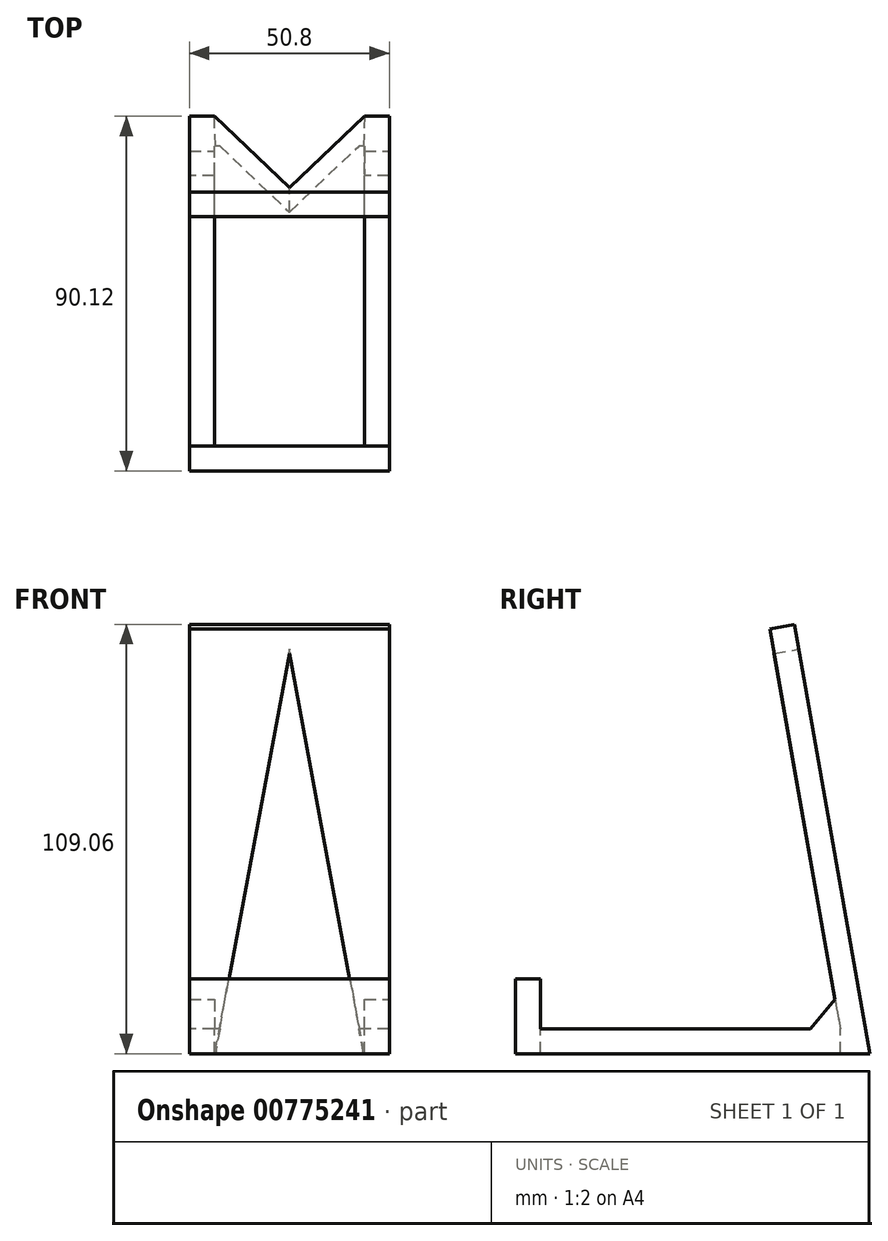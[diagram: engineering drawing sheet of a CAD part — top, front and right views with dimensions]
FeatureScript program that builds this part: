
annotation { "Feature Type Name" : "Feature", "Feature Type Description" : "" }
export const myFeature = defineFeature(function(context is Context, id is Id, definition is map)
    precondition{}
    {
        {
            var Q0;
            Q0=qCreatedBy(makeId("Right.planeOp"),FACE);
            var sketch = newSketch(context, id + "F0", { "sketchPlane" : qUnion([Q0])});
            skLineSegment(sketch, "E0", {"start": v(-39.61, -22.49) * mm, "end": v(36.59, -22.49) * mm});
            skLineSegment(sketch, "E1", {"start": v(36.59, -22.49) * mm, "end": v(18.67, 79.11) * mm});
            skLineSegment(sketch, "E2", {"start": v(-39.61, -22.49) * mm, "end": v(-39.61, -9.79) * mm});
            skLineSegment(sketch, "E3.0", {"start": v(-45.96, -28.84) * mm, "end": v(-45.96, -9.79) * mm});
            skLineSegment(sketch, "E3.1", {"start": v(-45.96, -28.84) * mm, "end": v(44.16, -28.84) * mm});
            skLineSegment(sketch, "E3.2", {"start": v(44.16, -28.84) * mm, "end": v(24.93, 80.22) * mm});
            skLineSegment(sketch, "E4", {"start": v(-45.96, -9.79) * mm, "end": v(-39.61, -9.79) * mm});
            skLineSegment(sketch, "E5", {"start": v(18.67, 79.11) * mm, "end": v(24.93, 80.22) * mm});
            skSolve(sketch);
        }
        {
            var Q0;
            Q0 = qSketchRegion(id + "F0", true);
            extrude(context, id + "F1", {"entities" : qUnion([Q0]), "depth" : 50.8 * mm, "offsetDistance" : 25.4 * mm});
        }
        {
            var Q0;
            Q0=makeQuery(id+"F1.opExtrude","SWEPT_FACE",FACE,{"disambiguationData":[OSD([sQuery(id+"F0.wireOp",EDGE,"E0")])]});
            var sketch = newSketch(context, id + "F2", { "sketchPlane" : qUnion([Q0])});
            skLineSegment(sketch, "E6.bottom", {"start": v(6.35, -39.61) * mm, "end": v(44.45, -39.61) * mm});
            skLineSegment(sketch, "E6.top", {"start": v(6.35, 36.59) * mm, "end": v(44.45, 36.59) * mm});
            skLineSegment(sketch, "E6.left", {"start": v(6.35, -39.61) * mm, "end": v(6.35, 36.59) * mm});
            skLineSegment(sketch, "E6.right", {"start": v(44.45, -39.61) * mm, "end": v(44.45, 36.59) * mm});
            skSolve(sketch);
        }
        {
            var Q0;
            Q0 = qSketchRegion(id + "F2", true);
            extrude(context, id + "F3", {"entities" : qUnion([Q0]), "operationType" : NewBodyOperationType.REMOVE, "oppositeDirection" : true, "depth" : 25.4 * mm, "offsetDistance" : 25.4 * mm});
        }
        {
            var Q0;
            Q0=makeQuery(id+"F1.opExtrude","SWEPT_FACE",FACE,{"disambiguationData":[OSD([sQuery(id+"F0.wireOp",EDGE,"E3.2")])]});
            var sketch = newSketch(context, id + "F4", { "sketchPlane" : qUnion([Q0])});
            skLineSegment(sketch, "E7", {"start": v(-44.45, -36.07) * mm, "end": v(-25.4, 68.32) * mm});
            skLineSegment(sketch, "E8", {"start": v(-25.4, 68.32) * mm, "end": v(-6.35, -36.07) * mm});
            skLineSegment(sketch, "E9", {"start": v(-6.35, -36.07) * mm, "end": v(-44.45, -36.07) * mm});
            skSolve(sketch);
        }
        {
            var Q0;
            Q0 = qSketchRegion(id + "F4", true);
            extrude(context, id + "F5", {"entities" : qUnion([Q0]), "operationType" : NewBodyOperationType.REMOVE, "oppositeDirection" : true, "depth" : 25.4 * mm, "offsetDistance" : 25.4 * mm});
        }
        {
            var Q0;
            {var subQ0=sQuery(id+"F0.wireOp",EDGE,"E1");var subQ1=sQuery(id+"F0.wireOp",EDGE,"E0");Q0=makeQuery(id+"F3.boolean.opBoolean","SPLIT",EDGE,{"disambiguationData":[TD([makeQuery(id+"F3.opExtrude","SWEPT_FACE",FACE,{"disambiguationData":[OSD([sQuery(id+"F2.wireOp",EDGE,"E6.left")])]})])],"derivedFrom":makeQuery(id+"F1.opExtrude","SWEPT_EDGE",EDGE,{"disambiguationData":[OSD([subQ1,subQ0])]})});}
            var Q1;
            {var subQ0=sQuery(id+"F0.wireOp",EDGE,"E1");var subQ1=sQuery(id+"F0.wireOp",EDGE,"E0");Q1=makeQuery(id+"F3.boolean.opBoolean","SPLIT",EDGE,{"disambiguationData":[TD([makeQuery(id+"F3.opExtrude","SWEPT_FACE",FACE,{"disambiguationData":[OSD([sQuery(id+"F2.wireOp",EDGE,"E6.right")])]})])],"derivedFrom":makeQuery(id+"F1.opExtrude","SWEPT_EDGE",EDGE,{"disambiguationData":[OSD([subQ1,subQ0])]})});}
            chamfer(context, id + "F6", {"entities" : qUnion([Q0, Q1]), "width" : 6.35 * mm, "tangentPropagation" : true});
        }
    });
